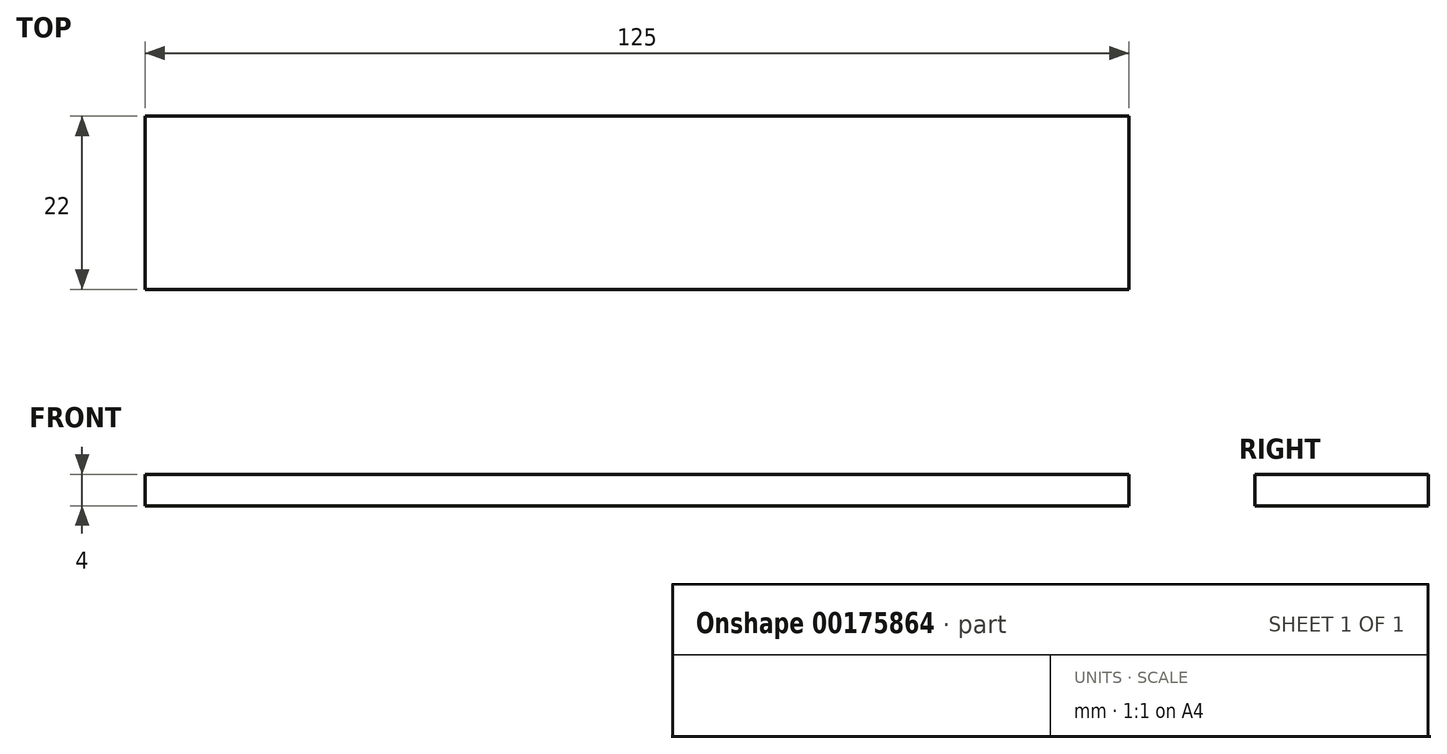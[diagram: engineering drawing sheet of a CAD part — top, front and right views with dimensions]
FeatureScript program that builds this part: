
annotation { "Feature Type Name" : "Feature", "Feature Type Description" : "" }
export const myFeature = defineFeature(function(context is Context, id is Id, definition is map)
    precondition{}
    {
        {
            var Q0;
            Q0=qCreatedBy(makeId("Top.planeOp"),FACE);
            var sketch = newSketch(context, id + "F0", { "sketchPlane" : qUnion([Q0])});
            skLineSegment(sketch, "E0.bottom", {"start": v(-120.49, -13.6) * mm, "end": v(4.51, -13.6) * mm});
            skLineSegment(sketch, "E0.top", {"start": v(-120.49, -35.6) * mm, "end": v(4.51, -35.6) * mm});
            skLineSegment(sketch, "E0.left", {"start": v(-120.49, -13.6) * mm, "end": v(-120.49, -35.6) * mm});
            skLineSegment(sketch, "E0.right", {"start": v(4.51, -13.6) * mm, "end": v(4.51, -35.6) * mm});
            skSolve(sketch);
        }
        {
            var Q0;
            Q0=qSketchRegion(id+"F0",true);
            extrude(context, id + "F1", {"entities" : qUnion([Q0]), "depth" : 4 * mm});
        }
    });
